# Revit family: WD2S-Down
name_source: partatom
category: Lighting Fixtures
units: mm (PartAtom-declared; Revit-internal decimal feet)

## family parameters
Always vertical = No
Cut with Voids When Loaded = No
Host = Wall
Light Source = Yes
OmniClass Number = 23.80.70.14.11.17
OmniClass Title = Wall or Ceiling Mounted External Lighting
Part Type = Normal
Room Calculation Point = No
Round Connector Dimension = Use Diameter
Shared = Yes

## types (6) — shared parameters
Apparent Load = 0 VA
Assembly Code = D5020200
Color Filter = 16777215
Colour Option = WD : White
Description = Wall Mounted Luminaire
Dimming Lamp Color Temperature Shift = <None>
Emit Shape Visible in Rendering = No
Emit from Rectangle Length = 4 "
Emit from Rectangle Width = 9 "
Lamp = 24 LEDs
Load Classification = Lighting
Manufacturer = Kim Lighting
MasterFormat Title = Parking Lighting, Site Lighting
Model = WD2S-Down
Note Text = LF
Note Visible = Yes
Number of Poles = 1
OmniClass Number = 23-80 70 14 11 17
OmniClass Title = Wall or Ceiling Mounted External Lighting
Photometric Notes = More IES files download on Photometric Web Link
Power Factor = 1
Series = Wall Director
Tilt Angle = 90.00°
Type Comments = Lighting Fixture
URL = https://www.currentlighting.com
Voltage = 120 V
Wattage Comments = 30, 40, 60 & 75W
zero-valued in all types: Default Elevation

## per-type parameters (varying)
| type | Distribution | Light Engine | Mounting Height | Photometric Web File | Watts |
| WDS-D-24L-59-4K7-3 | Type III | 4000K/70CRI | 72 " | WDS-D-24L-59-4K7-3.IES | 59 W |
| WDS-D-24L-30-3K7-WG | Wall Graze | 3000K/70CRI | 72 " | WDS-D-24L-30-3K7-WG.IES | 29 W |
| WDS-D-24L-42-3K7-4F | Type IV Forward | 3000K/70CRI | 72 " | WDS-D-24L-42-3K7-4F.IES | 42 W |
| WDS-D-24L-59-5K7-1 | Type I | 5000K/70CRI | 72 " | WDS-D-24L-59-5K7-1.ies | 59 W |
| WDS-D-24L-74-4K7-3 | Type III | 4000K/70CRI | 108 " | WDS-D-24L-74-4K7-3.IES | 74 W |
| WDS-D-24L-30-3K7-3 | Type III | 3000K/70CRI | 72 " | WDS-D-24L-30-3K7-3.IES | 29 W |

## geometry (parser evidence)
native form markers: Blend x6, Sweep x3
no freeform markers — native parametric forms only
